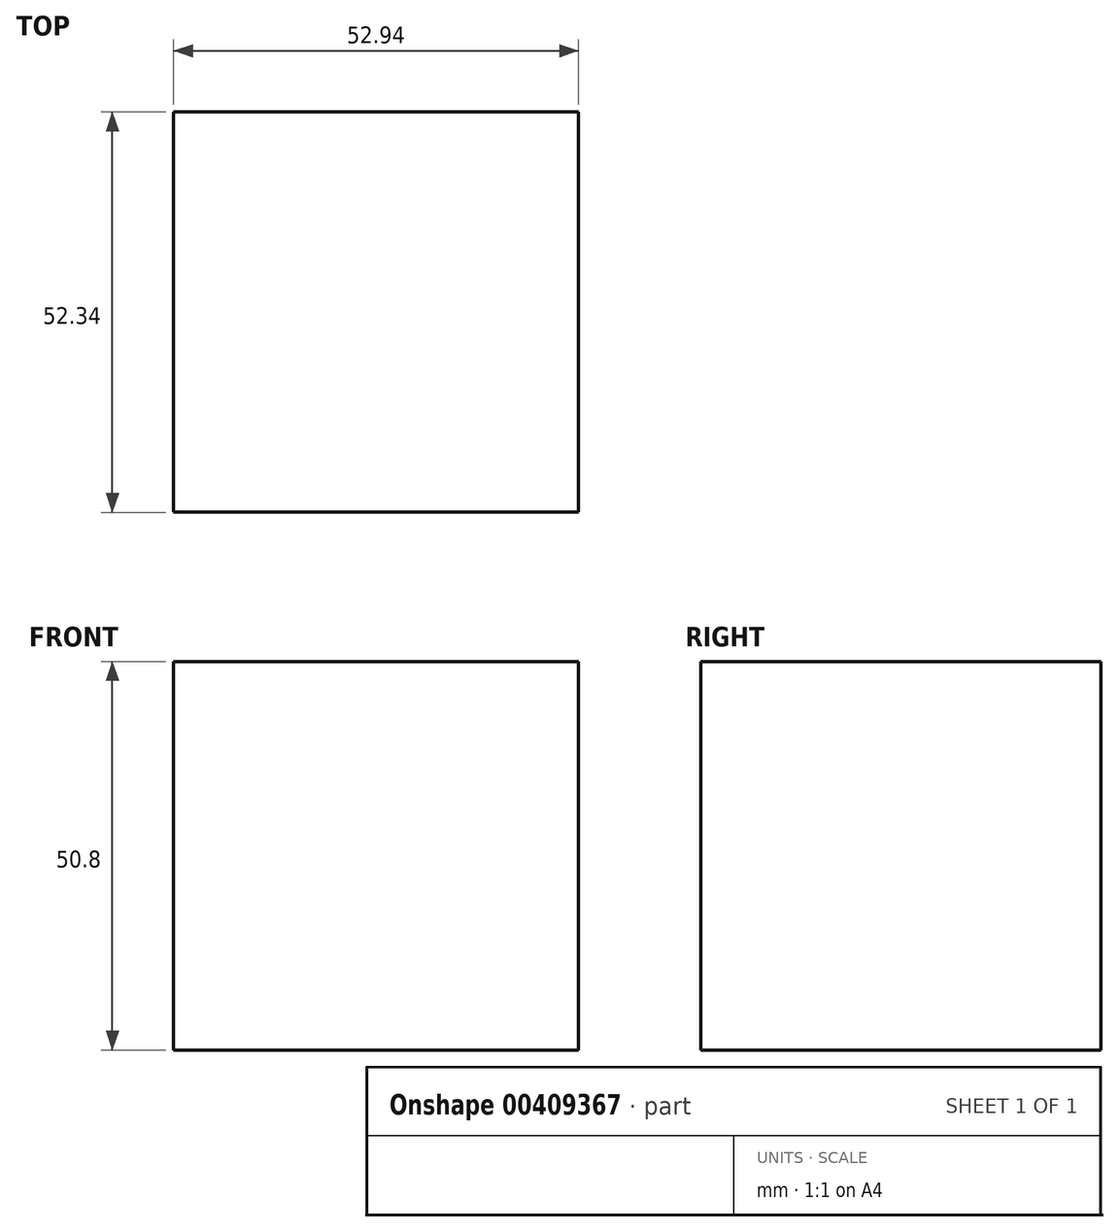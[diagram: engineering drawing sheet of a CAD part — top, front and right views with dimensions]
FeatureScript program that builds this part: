
annotation { "Feature Type Name" : "Feature", "Feature Type Description" : "" }
export const myFeature = defineFeature(function(context is Context, id is Id, definition is map)
    precondition{}
    {
        {
            var Q0;
            Q0=qCreatedBy(makeId("Top.planeOp"),FACE);
            var sketch = newSketch(context, id + "F0", { "sketchPlane" : qUnion([Q0])});
            skLineSegment(sketch, "E0.bottom", {"start": v(-18.05, 61.36) * mm, "end": v(-70.99, 61.36) * mm});
            skLineSegment(sketch, "E0.top", {"start": v(-18.05, 9.02) * mm, "end": v(-70.99, 9.02) * mm});
            skLineSegment(sketch, "E0.left", {"start": v(-18.05, 61.36) * mm, "end": v(-18.05, 9.02) * mm});
            skLineSegment(sketch, "E0.right", {"start": v(-70.99, 61.36) * mm, "end": v(-70.99, 9.02) * mm});
            skPoint(sketch, "E0.middle", {"position": v(-44.52, 35.2) * mm});
            skSolve(sketch);
        }
        {
            var Q0;
            Q0 = qSketchRegion(id + "F0", true);
            extrude(context, id + "F1", {"entities" : qUnion([Q0]), "depth" : 50.8 * mm});
        }
    });
